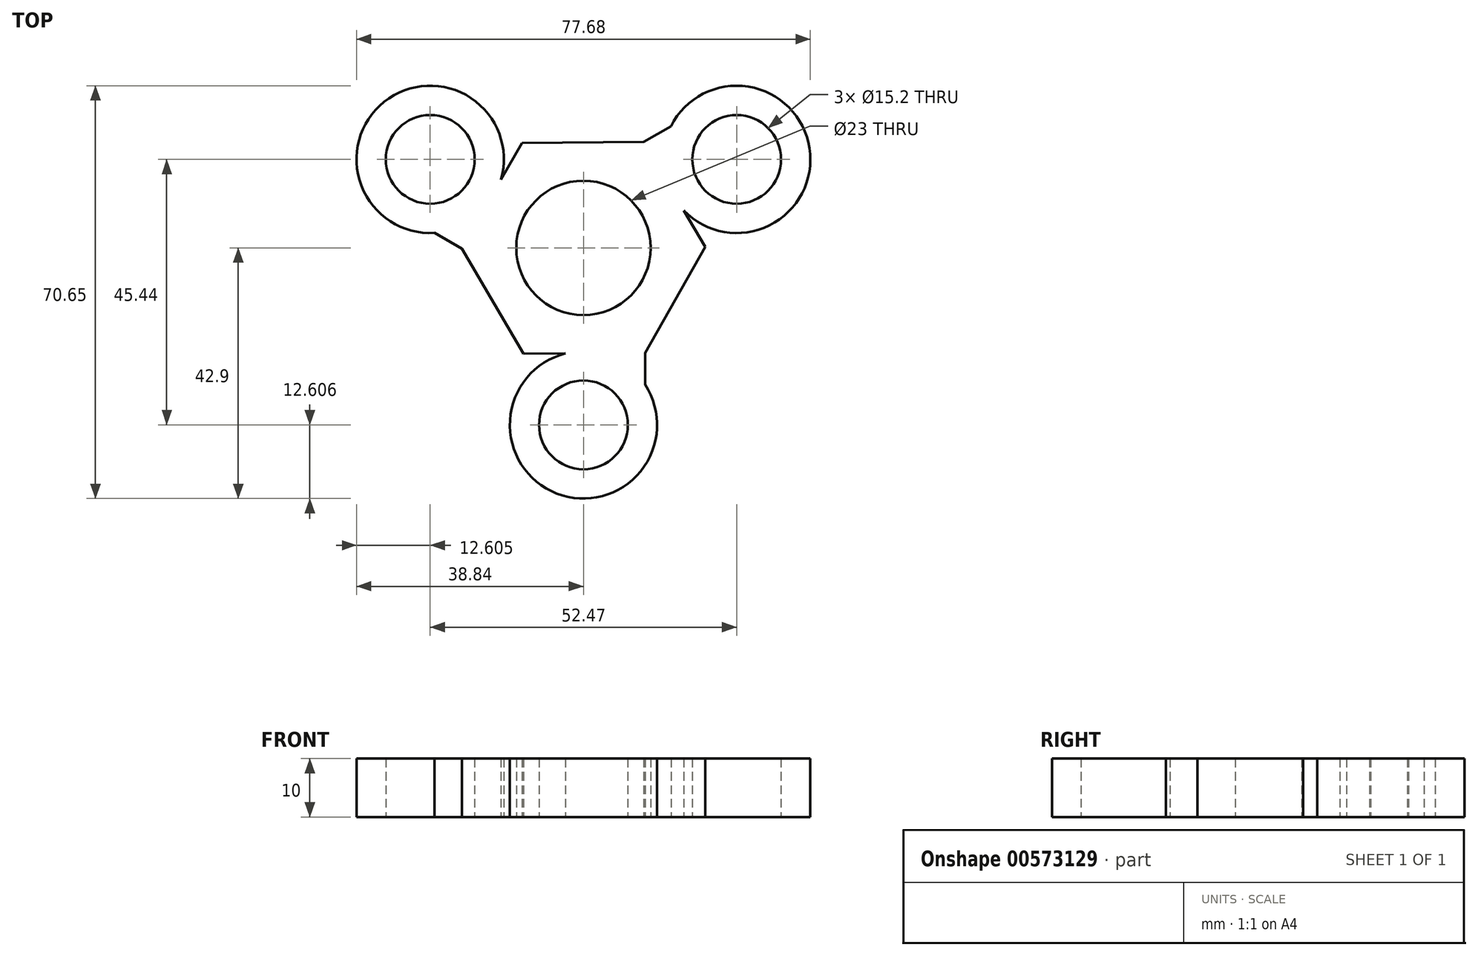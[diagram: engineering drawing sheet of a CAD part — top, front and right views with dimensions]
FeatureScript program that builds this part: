
annotation { "Feature Type Name" : "Feature", "Feature Type Description" : "" }
export const myFeature = defineFeature(function(context is Context, id is Id, definition is map)
    precondition{}
    {
        {
            var Q0;
            Q0=qCreatedBy(makeId("Top.planeOp"),FACE);
            var sketch = newSketch(context, id + "F0", { "sketchPlane" : qUnion([Q0])});
            skCircle(sketch, "E0", {"center": v(0, 0) * mm, "radius": 11.5 * mm});
            skCircle(sketch, "E1.cCircle", {"center": v(0, 0) * mm, "radius": 20.84 * mm, "construction": true});
            skLineSegment(sketch, "E1.0", {"start": v(-10.3, -18.12) * mm, "end": v(-20.84, -0.15) * mm});
            skLineSegment(sketch, "E1.1", {"start": v(-20.84, -0.15) * mm, "end": v(-10.55, 17.97) * mm});
            skLineSegment(sketch, "E1.2", {"start": v(-10.55, 17.97) * mm, "end": v(10.3, 18.12) * mm});
            skLineSegment(sketch, "E1.3", {"start": v(10.3, 18.12) * mm, "end": v(20.84, 0.15) * mm});
            skLineSegment(sketch, "E1.4", {"start": v(20.84, 0.15) * mm, "end": v(10.55, -17.97) * mm});
            skLineSegment(sketch, "E1.5", {"start": v(10.55, -17.97) * mm, "end": v(-10.3, -18.12) * mm});
            skCircle(sketch, "E2", {"center": v(0, -30.3) * mm, "radius": 7.6 * mm});
            skCircle(sketch, "E3.1.0", {"center": v(26.24, 15.15) * mm, "radius": 7.6 * mm});
            skCircle(sketch, "E3.2.0", {"center": v(-26.24, 15.15) * mm, "radius": 7.6 * mm});
            skCircle(sketch, "E4", {"center": v(0, -30.3) * mm, "radius": 12.6 * mm});
            skLineSegment(sketch, "E5", {"start": v(10.55, -17.97) * mm, "end": v(10.55, -23.38) * mm});
            skLineSegment(sketch, "E6.MirrorCS", {"start": v(-10.55, -17.97) * mm, "end": v(-10.55, -23.38) * mm});
            skCircle(sketch, "E7.1.0", {"center": v(26.24, 15.15) * mm, "radius": 12.6 * mm});
            skCircle(sketch, "E7.2.0", {"center": v(-26.24, 15.15) * mm, "radius": 12.6 * mm});
            skLineSegment(sketch, "E8.1.0", {"start": v(10.3, 18.12) * mm, "end": v(14.98, 20.82) * mm});
            skLineSegment(sketch, "E8.1.1", {"start": v(20.84, -0.15) * mm, "end": v(25.52, 2.56) * mm});
            skLineSegment(sketch, "E8.2.0", {"start": v(-20.84, -0.15) * mm, "end": v(-25.52, 2.56) * mm});
            skLineSegment(sketch, "E8.2.1", {"start": v(-10.3, 18.12) * mm, "end": v(-14.98, 20.82) * mm});
            skSolve(sketch);
        }
        {
            var Q0;
            Q0 = qSketchRegion(id + "F0", true);
            extrude(context, id + "F1", {"entities" : qUnion([Q0]), "depth" : 10 * mm, "offsetDistance" : 25.4 * mm});
        }
    });
